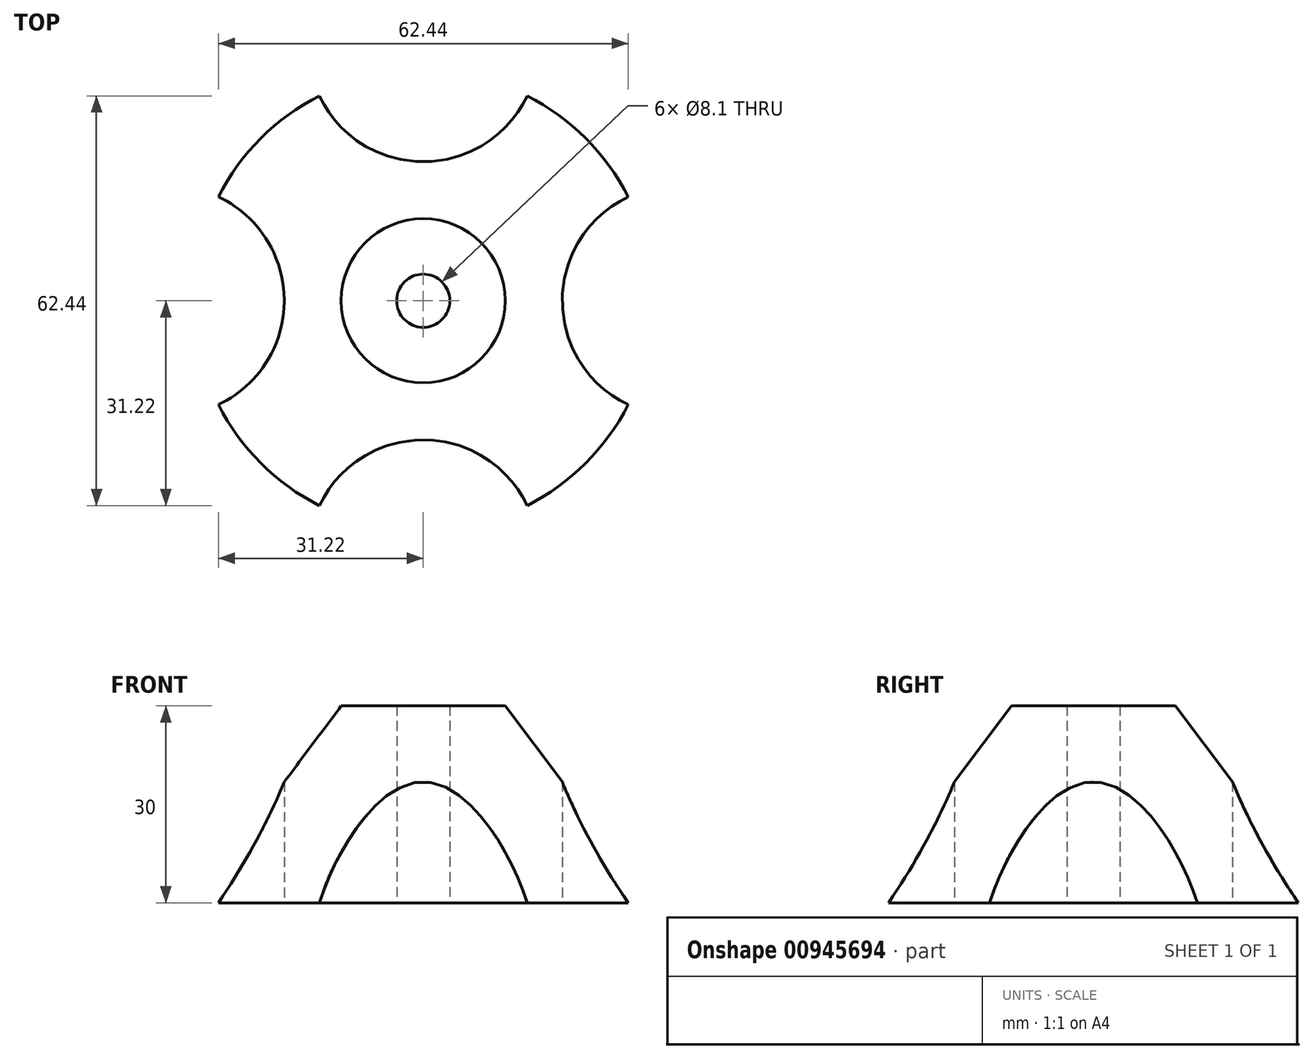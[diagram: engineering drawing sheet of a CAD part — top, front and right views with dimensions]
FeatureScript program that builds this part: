
annotation { "Feature Type Name" : "Feature", "Feature Type Description" : "" }
export const myFeature = defineFeature(function(context is Context, id is Id, definition is map)
    precondition{}
    {
        {
            var Q0;
            Q0=qCreatedBy(makeId("Front.planeOp"),FACE);
            var sketch = newSketch(context, id + "F0", { "sketchPlane" : qUnion([Q0])});
            skLineSegment(sketch, "E0", {"start": v(-35, 0) * mm, "end": v(-12.5, 30) * mm});
            skLineSegment(sketch, "E1", {"start": v(0, 0) * mm, "end": v(0, 30) * mm});
            skLineSegment(sketch, "E2", {"start": v(0, 30) * mm, "end": v(-12.5, 30) * mm});
            skLineSegment(sketch, "E3", {"start": v(0, 0) * mm, "end": v(-35, 0) * mm});
            skSolve(sketch);
        }
        {
            var Q0;
            Q0=makeQuery(id+"F0.imprint","IMPRINT",FACE,{"disambiguationData":[TD([[makeQuery(id+"F0.imprint","IMPRINT",EDGE,{"derivedFrom":sQuery(id+"F0.wireOp",EDGE,"E0")}),-1.0]])]});
            var Q1;
            Q1=sQuery(id+"F0.wireOp",EDGE,"E1");
            revolve(context, id + "F1", {"surfaceOperationType" : NewSurfaceOperationType.NEW, "entities" : qUnion([Q0]), "axis" : qUnion([Q1]), "revolveType" : RevolveType.FULL});
        }
        {
            var Q0;
            Q0=qCreatedBy(makeId("Top.planeOp"),FACE);
            var sketch = newSketch(context, id + "F2", { "sketchPlane" : qUnion([Q0])});
            skCircle(sketch, "E4", {"center": v(0, 0) * mm, "radius": 4.05 * mm});
            skSolve(sketch);
        }
        {
            var Q0;
            Q0=qSketchRegion(id+"F2",true);
            extrude(context, id + "F3", {"entities" : qUnion([Q0]), "operationType" : NewBodyOperationType.REMOVE, "oppositeDirection" : true, "depth" : -30 * mm, "offsetDistance" : 25 * mm});
        }
        {
            var Q0;
            Q0=qCreatedBy(makeId("Top.planeOp"),FACE);
            var sketch = newSketch(context, id + "F4", { "sketchPlane" : qUnion([Q0])});
            skCircle(sketch, "E5", {"center": v(0, 38.68) * mm, "radius": 17.5 * mm});
            skCircle(sketch, "E6.1.0", {"center": v(-38.68, 0) * mm, "radius": 17.5 * mm});
            skCircle(sketch, "E6.2.0", {"center": v(0, -38.68) * mm, "radius": 17.5 * mm});
            skCircle(sketch, "E6.3.0", {"center": v(38.68, 0) * mm, "radius": 17.5 * mm});
            skPoint(sketch, "E6.center", {"position": v(0, 0) * mm});
            skSolve(sketch);
        }
        {
            var Q0;
            Q0=qSketchRegion(id+"F4",true);
            extrude(context, id + "F5", {"entities" : qUnion([Q0]), "operationType" : NewBodyOperationType.REMOVE, "oppositeDirection" : true, "depth" : -25 * mm, "offsetDistance" : 25 * mm});
        }
    });
